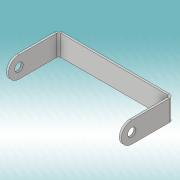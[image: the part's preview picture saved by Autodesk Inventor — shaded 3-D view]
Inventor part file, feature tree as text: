
AUTODESK INVENTOR PART (.ipt)
format: ipt  version: 2019 (Build 230136000, 136)  size: 167,936 bytes
history: native  units: in
note: dims shown in document units (in); Inventor stores cm internally (conversion verified against a paired STEP export)
features: sheet_metal_op x6, sketch x5, other x4, extrude x1
ambient origin geometry x8: Origin, YZ Plane, XZ Plane, XY Plane, X Axis, Y Axis, Z Axis, Center Point
bodies: Solid1 (feature_tree)
feature tree (16):
  extrude  "Extrusion1"  Depth=0.0787in TaperAngle=0.0deg
  sheet_metal_op  "Flange1"
  sheet_metal_op  "Flange2"
  sketch  "Sketch1"  dims[d0=2.1654in d4=0.0787in d5=0.0in]
  sketch  "Sketch2"  dims[d6=0.7874in]
  other  "Plate1"
  sheet_metal_op  "Bend1"
  sheet_metal_op  "Corner1"
  sketch  "Sketch3"  dims[d7=0.0787in]
  other  "Plate2"
  sheet_metal_op  "Bend2"
  sheet_metal_op  "Corner2"
  sketch  "Sketch5"  dims[d8=0.0787in]
  sketch  "Sketch6"  dims[d9=0.0394in d10=0.1575in d11=0.0787in d12=1.9685in d13=90.0deg d14=0.0787in d15=0.315in d16=0.0787in d17=0.0787in d18=0.0787in d19=0.0394in d20=0.1575in d21=0.0787in d22=1.9685in d23=90.0deg d24=0.0787in d25=0.315in d26=0.0787in d27=0.0787in d38=0.3937in d39=0.3937in d40=0.3937in d41=0.0787in d42=0.0in d43=0.3937in d44=0.0787in d45=0.0in d46=0.315in d47=0.315in]
  other  "Cut1"
  other  "Cut2"
